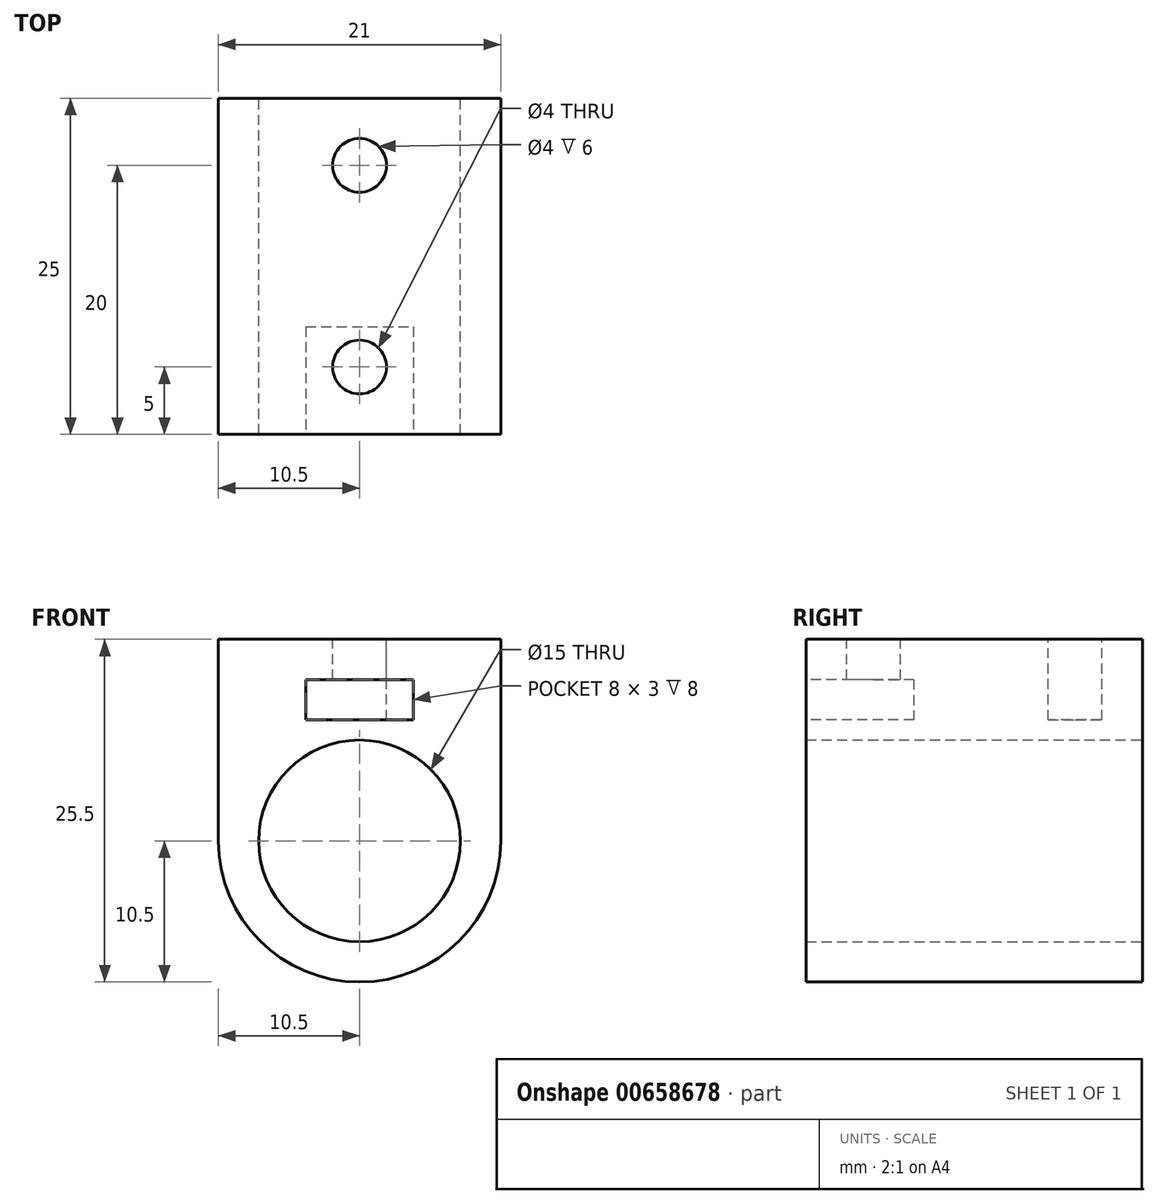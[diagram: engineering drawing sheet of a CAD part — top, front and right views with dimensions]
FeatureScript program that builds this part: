
annotation { "Feature Type Name" : "Feature", "Feature Type Description" : "" }
export const myFeature = defineFeature(function(context is Context, id is Id, definition is map)
    precondition{}
    {
        {
            var Q0;
            Q0=qCreatedBy(makeId("Front.planeOp"),FACE);
            var sketch = newSketch(context, id + "F0", { "sketchPlane" : qUnion([Q0])});
            skCircle(sketch, "E0", {"center": v(0, 0) * mm, "radius": 7.5 * mm});
            skCircle(sketch, "E1", {"center": v(0, 0) * mm, "radius": 10.5 * mm});
            skLineSegment(sketch, "E2.bottom", {"start": v(-10.5, 0) * mm, "end": v(10.5, 0) * mm});
            skLineSegment(sketch, "E2.top", {"start": v(-10.5, 15) * mm, "end": v(10.5, 15) * mm});
            skLineSegment(sketch, "E2.left", {"start": v(-10.5, 0) * mm, "end": v(-10.5, 15) * mm});
            skLineSegment(sketch, "E2.right", {"start": v(10.5, 0) * mm, "end": v(10.5, 15) * mm});
            skSolve(sketch);
        }
        {
            var Q0;
            Q0=makeQuery(id+"F0.imprint","IMPRINT",FACE,{"disambiguationData":[TD([[makeQuery(id+"F0.imprint","IMPRINT",EDGE,{"derivedFrom":sQuery(id+"F0.wireOp",EDGE,"E2.top")}),-1.0]])]});
            var Q1;
            {var subQ0=sQuery(id+"F0.wireOp",EDGE,"E2.bottom");var subQ1=sQuery(id+"F0.wireOp",EDGE,"E0");var subQ2=makeQuery(id+"F0.imprint","INTERSECT",VERTEX,{"disambiguationData":[OD(0.0)],"derivedFrom":[subQ1,subQ0]});Q1=makeQuery(id+"F0.imprint","IMPRINT",FACE,{"disambiguationData":[TD([[makeQuery(id+"F0.imprint","IMPRINT",EDGE,{"disambiguationData":[TD([[subQ2,1.0]])],"derivedFrom":subQ1}),-1.0]])]});}
            var Q2;
            {var subQ0=sQuery(id+"F0.wireOp",EDGE,"E2.bottom");var subQ1=sQuery(id+"F0.wireOp",EDGE,"E0");var subQ2=makeQuery(id+"F0.imprint","INTERSECT",VERTEX,{"disambiguationData":[OD(0.0)],"derivedFrom":[subQ1,subQ0]});Q2=makeQuery(id+"F0.imprint","IMPRINT",FACE,{"disambiguationData":[TD([[makeQuery(id+"F0.imprint","IMPRINT",EDGE,{"disambiguationData":[TD([[subQ2,-1.0]])],"derivedFrom":subQ1}),-1.0]])]});}
            extrude(context, id + "F1", {"entities" : qUnion([Q0, Q1, Q2]), "depth" : 25 * mm});
        }
        {
            var Q0;
            Q0=makeQuery(id+"F1.opExtrude","SWEPT_FACE",FACE,{"disambiguationData":[OSD([sQuery(id+"F0.wireOp",EDGE,"E2.top")])]});
            var sketch = newSketch(context, id + "F2", { "sketchPlane" : qUnion([Q0])});
            skCircle(sketch, "E3", {"center": v(0, -5) * mm, "radius": 2 * mm});
            skCircle(sketch, "E4", {"center": v(0, -20) * mm, "radius": 2 * mm});
            skSolve(sketch);
        }
        {
            var Q0;
            Q0=makeQuery(id+"F2.imprint","IMPRINT",FACE,{"disambiguationData":[TD([[makeQuery(id+"F2.imprint","IMPRINT",EDGE,{"derivedFrom":sQuery(id+"F2.wireOp",EDGE,"E3")}),1.0]])]});
            var Q1;
            Q1=makeQuery(id+"F2.imprint","IMPRINT",FACE,{"disambiguationData":[TD([[makeQuery(id+"F2.imprint","IMPRINT",EDGE,{"derivedFrom":sQuery(id+"F2.wireOp",EDGE,"E4")}),1.0]])]});
            extrude(context, id + "F3", {"entities" : qUnion([Q0, Q1]), "operationType" : NewBodyOperationType.REMOVE, "oppositeDirection" : true, "depth" : 6 * mm, "offsetDistance" : 25 * mm});
        }
        {
            var Q0;
            Q0=makeQuery(id+"F1.opExtrude","CAP_FACE",FACE,{"disambiguationData":[OSD([sQuery(id+"F0.wireOp",EDGE,"E0"),sQuery(id+"F0.wireOp",EDGE,"E1"),sQuery(id+"F0.wireOp",EDGE,"E2.top"),sQuery(id+"F0.wireOp",EDGE,"E2.left"),sQuery(id+"F0.wireOp",EDGE,"E2.right")])],"isStart":false});
            var sketch = newSketch(context, id + "F4", { "sketchPlane" : qUnion([Q0])});
            skLineSegment(sketch, "E5.bottom", {"start": v(-4, 12) * mm, "end": v(4, 12) * mm});
            skLineSegment(sketch, "E5.top", {"start": v(-4, 9) * mm, "end": v(4, 9) * mm});
            skLineSegment(sketch, "E5.left", {"start": v(-4, 12) * mm, "end": v(-4, 9) * mm});
            skLineSegment(sketch, "E5.right", {"start": v(4, 12) * mm, "end": v(4, 9) * mm});
            skSolve(sketch);
        }
        {
            var Q0;
            Q0=makeQuery(id+"F4.imprint","IMPRINT",FACE,{"disambiguationData":[TD([[makeQuery(id+"F4.imprint","IMPRINT",EDGE,{"derivedFrom":sQuery(id+"F4.wireOp",EDGE,"E5.bottom")}),-1.0]])]});
            extrude(context, id + "F5", {"entities" : qUnion([Q0]), "operationType" : NewBodyOperationType.REMOVE, "oppositeDirection" : true, "depth" : 8 * mm, "offsetDistance" : 25 * mm});
        }
        {
            var Q0;
            Q0=makeQuery(id+"F1.opExtrude","CAP_FACE",FACE,{"disambiguationData":[OSD([sQuery(id+"F0.wireOp",EDGE,"E0"),sQuery(id+"F0.wireOp",EDGE,"E1"),sQuery(id+"F0.wireOp",EDGE,"E2.top"),sQuery(id+"F0.wireOp",EDGE,"E2.left"),sQuery(id+"F0.wireOp",EDGE,"E2.right")])],"isStart":true});
            cPlane(context, id + "F6", {"entities" : qUnion([Q0]), "cplaneType" : CPlaneType.OFFSET, "offset" : 12.5 * mm, "oppositeDirection" : true, "width" : 150 * mm, "height" : 150 * mm});
        }
    });
